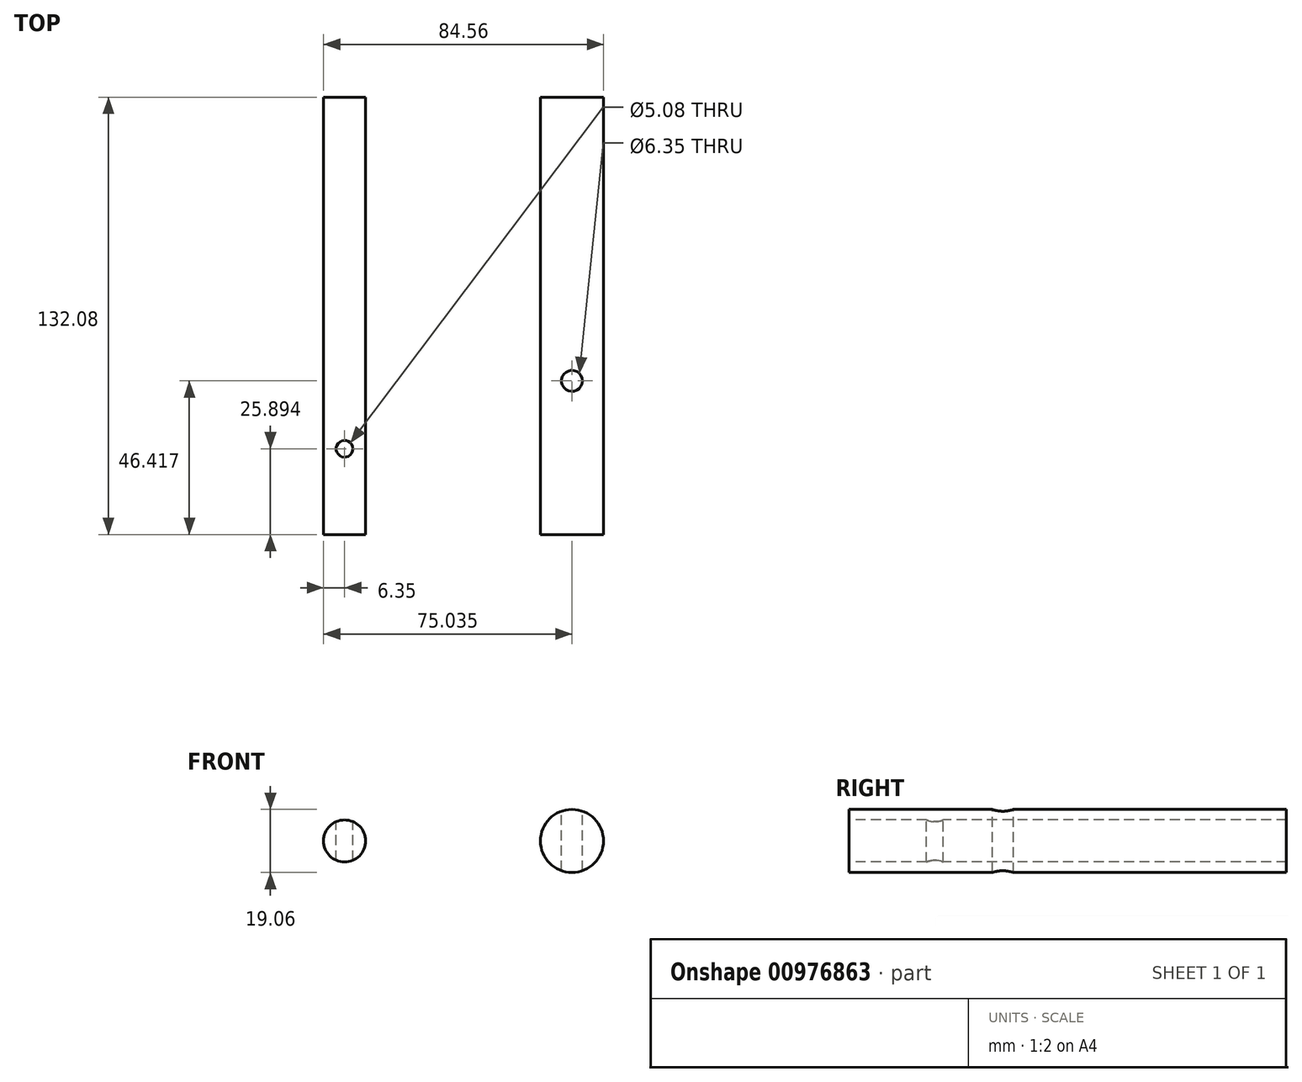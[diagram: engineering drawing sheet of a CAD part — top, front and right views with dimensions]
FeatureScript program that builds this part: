
annotation { "Feature Type Name" : "Feature", "Feature Type Description" : "" }
export const myFeature = defineFeature(function(context is Context, id is Id, definition is map)
    precondition{}
    {
        {
            var Q0;
            Q0=qCreatedBy(makeId("Front.planeOp"),FACE);
            var sketch = newSketch(context, id + "F0", { "sketchPlane" : qUnion([Q0])});
            skCircle(sketch, "E0", {"center": v(0, 0) * mm, "radius": 6.35 * mm});
            skCircle(sketch, "E1", {"center": v(68.69, 0) * mm, "radius": 9.53 * mm});
            skSolve(sketch);
        }
        {
            var Q0;
            Q0 = qSketchRegion(id + "F0", true);
            extrude(context, id + "F1", {"entities" : qUnion([Q0]), "oppositeDirection" : true, "depth" : 132.08 * mm, "offsetDistance" : 25.4 * mm});
        }
        {
            var Q0;
            Q0=qCreatedBy(makeId("Top.planeOp"),FACE);
            var sketch = newSketch(context, id + "F2", { "sketchPlane" : qUnion([Q0])});
            skCircle(sketch, "E2", {"center": v(0, 25.9) * mm, "radius": 2.54 * mm});
            skLineSegment(sketch, "E3.0", {"start": v(78.21, 0) * mm, "end": v(59.16, 0) * mm, "construction": true});
            skLineSegment(sketch, "E4", {"start": v(68.69, 0) * mm, "end": v(68.69, 46.42) * mm, "construction": true});
            skCircle(sketch, "E5", {"center": v(68.69, 46.42) * mm, "radius": 3.18 * mm});
            skSolve(sketch);
        }
        {
            var Q0;
            Q0 = qSketchRegion(id + "F2", true);
            extrude(context, id + "F3", {"entities" : qUnion([Q0]), "operationType" : NewBodyOperationType.REMOVE, "endBound" : BoundingType.THROUGH_ALL, "oppositeDirection" : true, "depth" : 25.4 * mm, "offsetDistance" : 25.4 * mm, "hasSecondDirection" : true, "secondDirectionBound" : BoundingType.THROUGH_ALL, "secondDirectionOppositeDirection" : false, "secondDirectionDepth" : 25.4 * mm});
        }
    });
